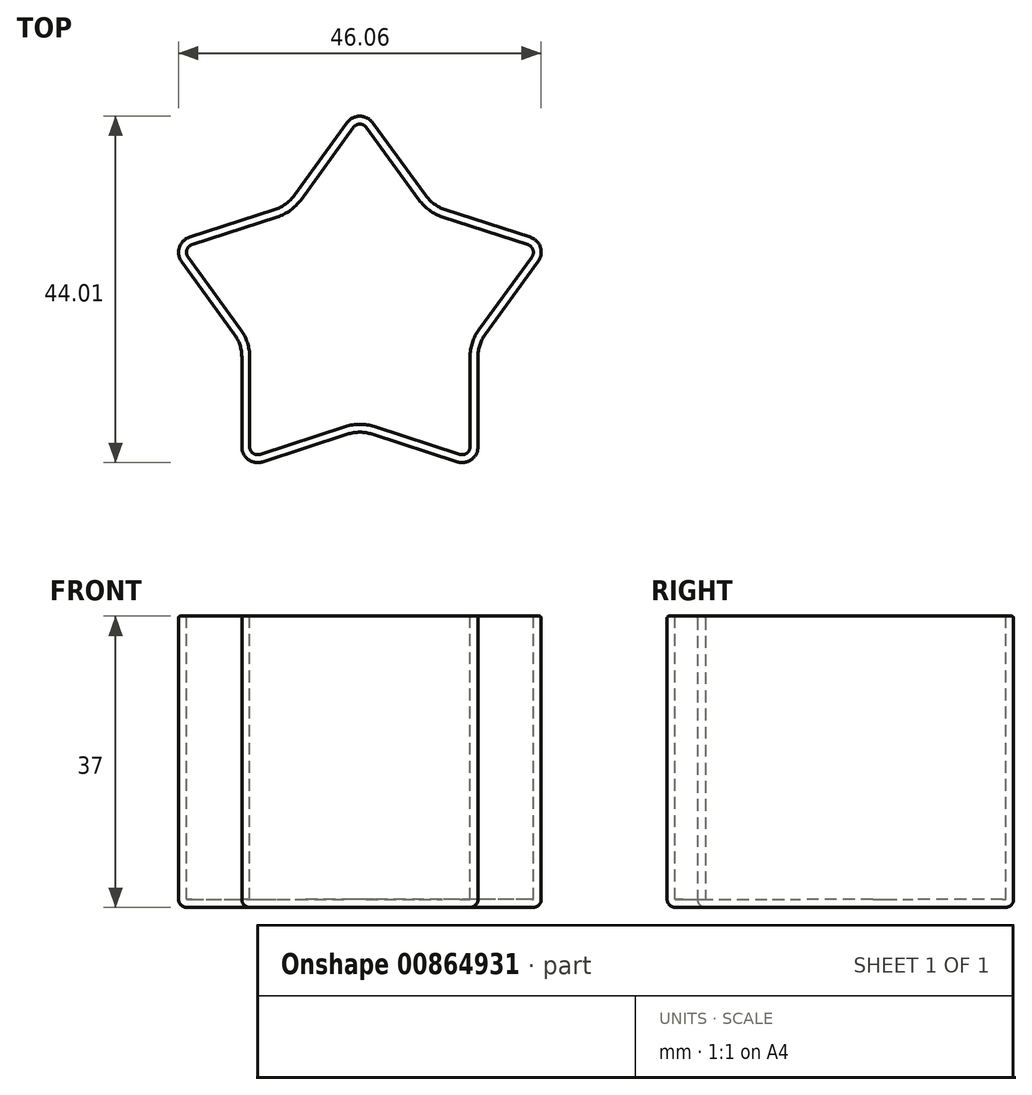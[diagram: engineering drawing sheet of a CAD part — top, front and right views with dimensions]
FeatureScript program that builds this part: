
annotation { "Feature Type Name" : "Feature", "Feature Type Description" : "" }
export const myFeature = defineFeature(function(context is Context, id is Id, definition is map)
    precondition{}
    {
        {
            var Q0;
            Q0=qCreatedBy(makeId("Top.planeOp"),FACE);
            var sketch = newSketch(context, id + "F0", { "sketchPlane" : qUnion([Q0])});
            skCircle(sketch, "E0.cCircle", {"center": v(0, 0) * mm, "radius": 20.65 * mm, "construction": true});
            skLineSegment(sketch, "E0.0", {"start": v(0, 25.52) * mm, "end": v(24.27, 7.89) * mm, "construction": true});
            skLineSegment(sketch, "E0.1", {"start": v(24.27, 7.89) * mm, "end": v(15, -20.65) * mm, "construction": true});
            skLineSegment(sketch, "E0.2", {"start": v(15, -20.65) * mm, "end": v(-15, -20.65) * mm, "construction": true});
            skLineSegment(sketch, "E0.3", {"start": v(-15, -20.65) * mm, "end": v(-24.27, 7.89) * mm, "construction": true});
            skLineSegment(sketch, "E0.4", {"start": v(-24.27, 7.89) * mm, "end": v(0, 25.52) * mm, "construction": true});
            skPoint(sketch, "E0.0.midPoint", {"position": v(12.14, 16.7) * mm});
            skLineSegment(sketch, "E1", {"start": v(-15, -20.65) * mm, "end": v(-15, -4.87) * mm});
            skLineSegment(sketch, "E2", {"start": v(15, -20.65) * mm, "end": v(15, -4.87) * mm});
            skLineSegment(sketch, "E3", {"start": v(-24.27, 7.89) * mm, "end": v(-15, -4.87) * mm});
            skLineSegment(sketch, "E4", {"start": v(24.27, 7.89) * mm, "end": v(15, -4.87) * mm});
            skLineSegment(sketch, "E5", {"start": v(-15, -20.65) * mm, "end": v(0, -15.77) * mm});
            skLineSegment(sketch, "E6", {"start": v(15, -20.65) * mm, "end": v(0, -15.77) * mm});
            skLineSegment(sketch, "E7", {"start": v(-24.27, 7.89) * mm, "end": v(-9.27, 12.76) * mm});
            skLineSegment(sketch, "E8", {"start": v(0, 25.52) * mm, "end": v(-9.27, 12.76) * mm});
            skLineSegment(sketch, "E9", {"start": v(0, 25.52) * mm, "end": v(9.27, 12.76) * mm});
            skLineSegment(sketch, "E10", {"start": v(24.27, 7.89) * mm, "end": v(9.27, 12.76) * mm});
            skSolve(sketch);
        }
        {
            var Q0;
            Q0=makeQuery(id+"F0.imprint","IMPRINT",FACE,{"disambiguationData":[TD([[makeQuery(id+"F0.imprint","IMPRINT",EDGE,{"derivedFrom":sQuery(id+"F0.wireOp",EDGE,"E1")}),-1.0]])]});
            extrude(context, id + "F1", {"entities" : qUnion([Q0]), "depth" : 37 * mm, "offsetDistance" : 25 * mm});
        }
        {
            var Q0;
            Q0=makeQuery(id+"F1.opExtrude","SWEPT_EDGE",EDGE,{"disambiguationData":[OSD([sQuery(id+"F0.wireOp",EDGE,"E9"),sQuery(id+"F0.wireOp",EDGE,"E10")])]});
            var Q1;
            Q1=makeQuery(id+"F1.opExtrude","SWEPT_EDGE",EDGE,{"disambiguationData":[OSD([sQuery(id+"F0.wireOp",EDGE,"E7"),sQuery(id+"F0.wireOp",EDGE,"E8")])]});
            var Q2;
            Q2=makeQuery(id+"F1.opExtrude","SWEPT_EDGE",EDGE,{"disambiguationData":[OSD([sQuery(id+"F0.wireOp",EDGE,"E1"),sQuery(id+"F0.wireOp",EDGE,"E3")])]});
            var Q3;
            Q3=makeQuery(id+"F1.opExtrude","SWEPT_EDGE",EDGE,{"disambiguationData":[OSD([sQuery(id+"F0.wireOp",EDGE,"E5"),sQuery(id+"F0.wireOp",EDGE,"E6")])]});
            var Q4;
            Q4=makeQuery(id+"F1.opExtrude","SWEPT_EDGE",EDGE,{"disambiguationData":[OSD([sQuery(id+"F0.wireOp",EDGE,"E2"),sQuery(id+"F0.wireOp",EDGE,"E4")])]});
            fillet(context, id + "F2", {"entities" : qUnion([Q0, Q1, Q2, Q3, Q4]), "radius" : 5 * mm, "tangentPropagation" : true, "allowEdgeOverflow" : false});
        }
        {
            var Q0;
            Q0=makeQuery(id+"F1.opExtrude","SWEPT_EDGE",EDGE,{"disambiguationData":[OSD([sQuery(id+"F0.wireOp",EDGE,"E1"),sQuery(id+"F0.wireOp",EDGE,"E5")])]});
            var Q1;
            Q1=makeQuery(id+"F1.opExtrude","SWEPT_EDGE",EDGE,{"disambiguationData":[OSD([sQuery(id+"F0.wireOp",EDGE,"E2"),sQuery(id+"F0.wireOp",EDGE,"E6")])]});
            var Q2;
            Q2=makeQuery(id+"F1.opExtrude","SWEPT_EDGE",EDGE,{"disambiguationData":[OSD([sQuery(id+"F0.wireOp",EDGE,"E4"),sQuery(id+"F0.wireOp",EDGE,"E10")])]});
            var Q3;
            Q3=makeQuery(id+"F1.opExtrude","SWEPT_EDGE",EDGE,{"disambiguationData":[OSD([sQuery(id+"F0.wireOp",EDGE,"E8"),sQuery(id+"F0.wireOp",EDGE,"E9")])]});
            var Q4;
            Q4=makeQuery(id+"F1.opExtrude","SWEPT_EDGE",EDGE,{"disambiguationData":[OSD([sQuery(id+"F0.wireOp",EDGE,"E3"),sQuery(id+"F0.wireOp",EDGE,"E7")])]});
            fillet(context, id + "F3", {"entities" : qUnion([Q0, Q1, Q2, Q3, Q4]), "radius" : 2 * mm, "tangentPropagation" : true, "allowEdgeOverflow" : false});
        }
        {
            var Q0;
            Q0=makeQuery(id+"F1.opExtrude","CAP_FACE",FACE,{"disambiguationData":[OSD([sQuery(id+"F0.wireOp",EDGE,"E1"),sQuery(id+"F0.wireOp",EDGE,"E2"),sQuery(id+"F0.wireOp",EDGE,"E3"),sQuery(id+"F0.wireOp",EDGE,"E4"),sQuery(id+"F0.wireOp",EDGE,"E5"),sQuery(id+"F0.wireOp",EDGE,"E6"),sQuery(id+"F0.wireOp",EDGE,"E7"),sQuery(id+"F0.wireOp",EDGE,"E8"),sQuery(id+"F0.wireOp",EDGE,"E9"),sQuery(id+"F0.wireOp",EDGE,"E10")])],"isStart":false});
            shell(context, id + "F4", {"entities" : qUnion([Q0]), "thickness" : 1 * mm});
        }
        {
            var Q0;
            Q0=makeQuery(id+"F1.opExtrude","CAP_FACE",FACE,{"disambiguationData":[OSD([sQuery(id+"F0.wireOp",EDGE,"E1"),sQuery(id+"F0.wireOp",EDGE,"E2"),sQuery(id+"F0.wireOp",EDGE,"E3"),sQuery(id+"F0.wireOp",EDGE,"E4"),sQuery(id+"F0.wireOp",EDGE,"E5"),sQuery(id+"F0.wireOp",EDGE,"E6"),sQuery(id+"F0.wireOp",EDGE,"E7"),sQuery(id+"F0.wireOp",EDGE,"E8"),sQuery(id+"F0.wireOp",EDGE,"E9"),sQuery(id+"F0.wireOp",EDGE,"E10")])],"isStart":true});
            fillet(context, id + "F5", {"entities" : qUnion([Q0]), "radius" : 1 * mm, "tangentPropagation" : true, "allowEdgeOverflow" : false});
        }
        {
            var Q0;
            Q0=makeQuery(id+"F1.opExtrude","CAP_FACE",FACE,{"disambiguationData":[OSD([sQuery(id+"F0.wireOp",EDGE,"E1"),sQuery(id+"F0.wireOp",EDGE,"E2"),sQuery(id+"F0.wireOp",EDGE,"E3"),sQuery(id+"F0.wireOp",EDGE,"E4"),sQuery(id+"F0.wireOp",EDGE,"E5"),sQuery(id+"F0.wireOp",EDGE,"E6"),sQuery(id+"F0.wireOp",EDGE,"E7"),sQuery(id+"F0.wireOp",EDGE,"E8"),sQuery(id+"F0.wireOp",EDGE,"E9"),sQuery(id+"F0.wireOp",EDGE,"E10")])],"isStart":false});
            fillet(context, id + "F6", {"entities" : qUnion([Q0]), "radius" : 0.25 * mm, "tangentPropagation" : true, "allowEdgeOverflow" : false});
        }
    });
